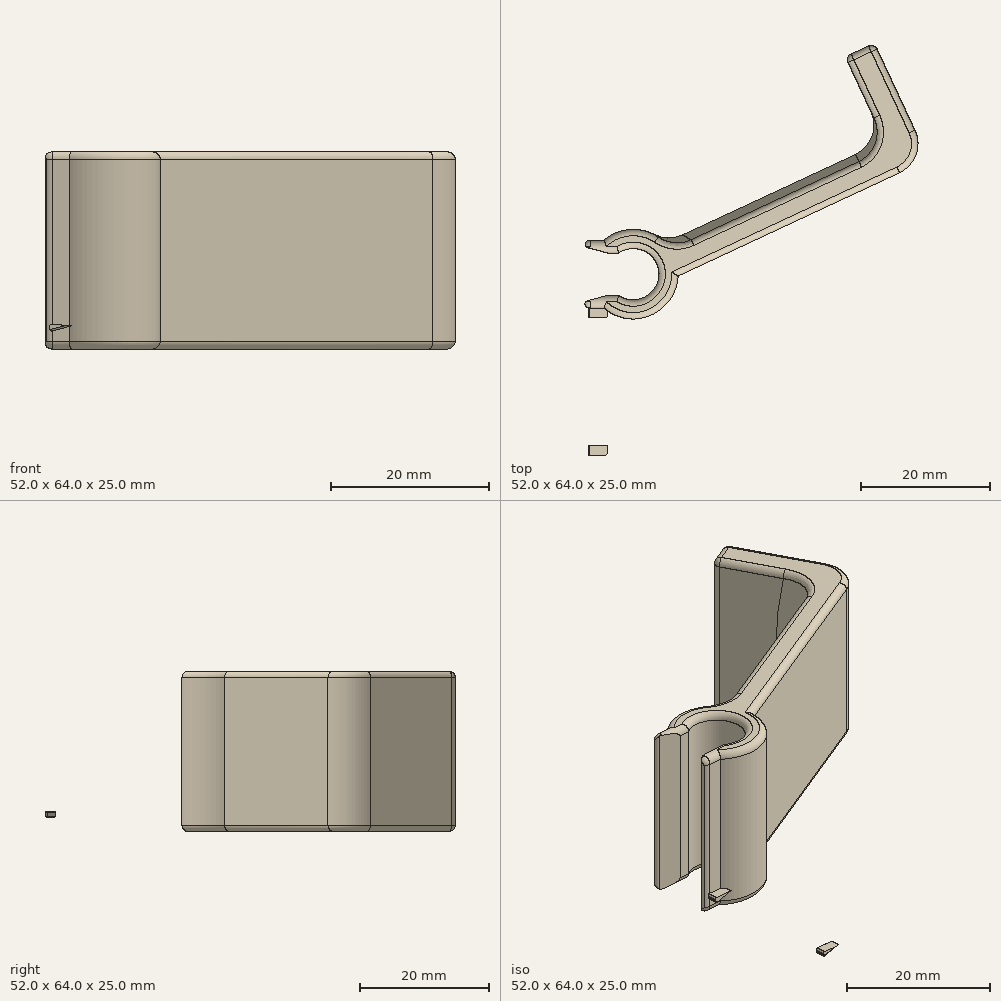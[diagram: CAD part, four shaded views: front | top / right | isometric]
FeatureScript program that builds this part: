
annotation { "Feature Type Name" : "Feature", "Feature Type Description" : "" }
export const myFeature = defineFeature(function(context is Context, id is Id, definition is map)
    precondition{}
    {
        {
            var Q0;
            Q0=qCreatedBy(makeId("Front.planeOp"),FACE);
            var sketch = newSketch(context, id + "F0", { "sketchPlane" : qUnion([Q0])});
            skCircle(sketch, "E0", {"center": v(0, 0) * mm, "radius": 7 * mm});
            skSolve(sketch);
        }
        {
            var Q0;
            Q0=makeQuery(id+"F0.imprint","IMPRINT",FACE,{"disambiguationData":[TD([[makeQuery(id+"F0.imprint","IMPRINT",EDGE,{"derivedFrom":sQuery(id+"F0.wireOp",EDGE,"E0")}),1.0]])]});
            extrude(context, id + "F1", {"entities" : qUnion([Q0]), "endBound" : BoundingType.SYMMETRIC, "depth" : 25 * mm, "offsetDistance" : 25 * mm});
        }
        {
            var Q0;
            Q0=makeQuery(id+"F1.opExtrude","CAP_FACE",FACE,{"disambiguationData":[OSD([sQuery(id+"F0.wireOp",EDGE,"E0")])],"isStart":false});
            var sketch = newSketch(context, id + "F2", { "sketchPlane" : qUnion([Q0])});
            skPoint(sketch, "E1", {"position": v(0, 0) * mm});
            skSolve(sketch);
        }
        {
            var Q0;
            Q0=sQuery(id+"F2.wireOp",VERTEX,"E1");
            var Q1;
            Q1=makeQuery(id+"F1.opExtrude","SWEPT_BODY",BODY,{"disambiguationData":[OSD([sQuery(id+"F0.wireOp",EDGE,"E0")])]});
            hole(context, id + "F3", {"style" : HoleStyle.SIMPLE, "endStyle" : HoleEndStyle.THROUGH, "holeDiameter" : 8 * mm, "isTappedThrough" : true, "tappedDepth" : 12 * mm, "tapClearance" : 3, "locations" : qUnion([Q0]), "scope" : qUnion([Q1]), "majorDiameter" : 5 * mm});
        }
        {
            var Q0;
            Q0=qCreatedBy(makeId("Right.planeOp"),FACE);
            var sketch = newSketch(context, id + "F4", { "sketchPlane" : qUnion([Q0])});
            skLineSegment(sketch, "E2.bottom", {"start": v(-25, 3.3) * mm, "end": v(25, 3.3) * mm});
            skLineSegment(sketch, "E2.top", {"start": v(-25, -3.3) * mm, "end": v(25, -3.3) * mm});
            skLineSegment(sketch, "E2.left", {"start": v(-25, 3.3) * mm, "end": v(-25, -3.3) * mm});
            skLineSegment(sketch, "E2.right", {"start": v(25, 3.3) * mm, "end": v(25, -3.3) * mm});
            skSolve(sketch);
        }
        {
            var Q0;
            Q0=makeQuery(id+"F4.imprint","IMPRINT",FACE,{"disambiguationData":[TD([[makeQuery(id+"F4.imprint","IMPRINT",EDGE,{"derivedFrom":sQuery(id+"F4.wireOp",EDGE,"E2.bottom")}),-1.0]])]});
            extrude(context, id + "F5", {"entities" : qUnion([Q0]), "operationType" : NewBodyOperationType.REMOVE, "oppositeDirection" : true, "depth" : 25 * mm, "offsetDistance" : 25 * mm});
        }
        {
            var Q0;
            Q0=makeQuery(id+"F1.opExtrude","SWEPT_BODY",BODY,{"disambiguationData":[OSD([sQuery(id+"F0.wireOp",EDGE,"E0")])]});
            var Q1;
            Q1=qCreatedBy(makeId("Right.planeOp"),FACE);
            transform(context, id + "F6", {"entities" : qUnion([Q0]), "transformType" : TransformType.TRANSLATION_DISTANCE, "transformDirection" : qUnion([Q1]), "distance" : 2.7 * mm, "makeCopy" : false});
        }
        {
            var Q0;
            Q0=qCreatedBy(makeId("Right.planeOp"),FACE);
            var sketch = newSketch(context, id + "F7", { "sketchPlane" : qUnion([Q0])});
            skLineSegment(sketch, "E3.bottom", {"start": v(12.5, 3.3) * mm, "end": v(-12.5, 3.3) * mm});
            skLineSegment(sketch, "E3.top", {"start": v(12.5, 5.3) * mm, "end": v(-12.5, 5.3) * mm});
            skLineSegment(sketch, "E3.left", {"start": v(12.5, 3.3) * mm, "end": v(12.5, 5.3) * mm});
            skLineSegment(sketch, "E3.right", {"start": v(-12.5, 3.3) * mm, "end": v(-12.5, 5.3) * mm});
            skLineSegment(sketch, "E4.bottom", {"start": v(-12.5, -3.3) * mm, "end": v(12.5, -3.3) * mm});
            skLineSegment(sketch, "E4.top", {"start": v(-12.5, -5.3) * mm, "end": v(12.5, -5.3) * mm});
            skLineSegment(sketch, "E4.left", {"start": v(-12.5, -3.3) * mm, "end": v(-12.5, -5.3) * mm});
            skLineSegment(sketch, "E4.right", {"start": v(12.5, -3.3) * mm, "end": v(12.5, -5.3) * mm});
            skSolve(sketch);
        }
        {
            var Q0;
            Q0=makeQuery(id+"F7.imprint","IMPRINT",FACE,{"disambiguationData":[TD([[makeQuery(id+"F7.imprint","IMPRINT",EDGE,{"derivedFrom":sQuery(id+"F7.wireOp",EDGE,"E3.bottom")}),-1.0]])]});
            var Q1;
            Q1=makeQuery(id+"F7.imprint","IMPRINT",FACE,{"disambiguationData":[TD([[makeQuery(id+"F7.imprint","IMPRINT",EDGE,{"derivedFrom":sQuery(id+"F7.wireOp",EDGE,"E4.bottom")}),-1.0]])]});
            extrude(context, id + "F8", {"entities" : qUnion([Q0, Q1]), "operationType" : NewBodyOperationType.ADD, "oppositeDirection" : true, "depth" : 5 * mm, "offsetDistance" : 25 * mm});
        }
        {
            var Q0;
            Q0=makeQuery(id+"F1.opExtrude","SWEPT_BODY",BODY,{"disambiguationData":[OSD([sQuery(id+"F0.wireOp",EDGE,"E0")])]});
            var Q1;
            Q1=qCreatedBy(makeId("Right.planeOp"),FACE);
            transform(context, id + "F9", {"entities" : qUnion([Q0]), "transformType" : TransformType.TRANSLATION_DISTANCE, "transformDirection" : qUnion([Q1]), "distance" : 8 * mm, "oppositeDirection" : true, "makeCopy" : false});
        }
        {
            var Q0;
            Q0=qCreatedBy(makeId("Right.planeOp"),FACE);
            var sketch = newSketch(context, id + "F10", { "sketchPlane" : qUnion([Q0])});
            skArc(sketch, "E5", {"start": v(12.5, 0) * mm, "mid": v(0, 1.45) * mm, "end": v(-12.5, 0) * mm});
            skLineSegment(sketch, "E6", {"start": v(-12.5, 0) * mm, "end": v(-12.5, -4.1) * mm});
            skLineSegment(sketch, "E7", {"start": v(-12.5, -4.1) * mm, "end": v(12.5, -4.1) * mm});
            skLineSegment(sketch, "E8", {"start": v(12.5, -4.1) * mm, "end": v(12.5, 0) * mm});
            skSolve(sketch);
        }
        {
            var Q0;
            Q0=makeQuery(id+"F10.imprint","IMPRINT",FACE,{"disambiguationData":[TD([[makeQuery(id+"F10.imprint","IMPRINT",EDGE,{"derivedFrom":sQuery(id+"F10.wireOp",EDGE,"E5")}),1.0]])]});
            extrude(context, id + "F11", {"entities" : qUnion([Q0]), "depth" : 45 * mm, "offsetDistance" : 25 * mm});
        }
        {
            var Q0;
            Q0=makeQuery(id+"F11.opExtrude","SWEPT_FACE",FACE,{"disambiguationData":[OSD([sQuery(id+"F10.wireOp",EDGE,"E7")])]});
            var sketch = newSketch(context, id + "F12", { "sketchPlane" : qUnion([Q0])});
            skLineSegment(sketch, "E9.bottom", {"start": v(45, 12.5) * mm, "end": v(40, 12.5) * mm});
            skLineSegment(sketch, "E9.top", {"start": v(45, -12.5) * mm, "end": v(40, -12.5) * mm});
            skLineSegment(sketch, "E9.left", {"start": v(45, 12.5) * mm, "end": v(45, -12.5) * mm});
            skLineSegment(sketch, "E9.right", {"start": v(40, 12.5) * mm, "end": v(40, -12.5) * mm});
            skSolve(sketch);
        }
        {
            var Q0;
            Q0=makeQuery(id+"F12.imprint","IMPRINT",FACE,{"disambiguationData":[TD([[makeQuery(id+"F12.imprint","IMPRINT",EDGE,{"derivedFrom":sQuery(id+"F12.wireOp",EDGE,"E9.bottom")}),1.0]])]});
            extrude(context, id + "F13", {"entities" : qUnion([Q0]), "operationType" : NewBodyOperationType.ADD, "oppositeDirection" : true, "depth" : 20 * mm, "offsetDistance" : 25 * mm});
        }
        {
            var Q0;
            Q0=makeQuery(id+"F11.opExtrude","SWEPT_BODY",BODY,{"disambiguationData":[OSD([sQuery(id+"F10.wireOp",EDGE,"E5"),sQuery(id+"F10.wireOp",EDGE,"E6"),sQuery(id+"F10.wireOp",EDGE,"E7"),sQuery(id+"F10.wireOp",EDGE,"E8")])]});
            var Q1;
            Q1=sQuery(id+"F10.wireOp",EDGE,"E7");
            transform(context, id + "F14", {"entities" : qUnion([Q0]), "transformType" : TransformType.ROTATION, "transformAxis" : qUnion([Q1]), "angle" : 25 * degree, "oppositeDirection" : true, "makeCopy" : false});
        }
        {
            var Q0;
            Q0=makeQuery(id+"F11.opExtrude","SWEPT_BODY",BODY,{"disambiguationData":[OSD([sQuery(id+"F10.wireOp",EDGE,"E5"),sQuery(id+"F10.wireOp",EDGE,"E6"),sQuery(id+"F10.wireOp",EDGE,"E7"),sQuery(id+"F10.wireOp",EDGE,"E8")])]});
            var Q1;
            Q1=qCreatedBy(makeId("Top.planeOp"),FACE);
            transform(context, id + "F15", {"entities" : qUnion([Q0]), "transformType" : TransformType.TRANSLATION_DISTANCE, "transformDirection" : qUnion([Q1]), "distance" : 3 * mm, "makeCopy" : false});
        }
        {
            var Q0;
            Q0=makeQuery(id+"F1.opExtrude","SWEPT_BODY",BODY,{"disambiguationData":[OSD([sQuery(id+"F0.wireOp",EDGE,"E0")])]});
            var Q1;
            Q1=makeQuery(id+"F11.opExtrude","SWEPT_BODY",BODY,{"disambiguationData":[OSD([sQuery(id+"F10.wireOp",EDGE,"E5"),sQuery(id+"F10.wireOp",EDGE,"E6"),sQuery(id+"F10.wireOp",EDGE,"E7"),sQuery(id+"F10.wireOp",EDGE,"E8")])]});
            booleanBodies(context, id + "F16", {"operationType" : BooleanOperationType.UNION, "tools" : qUnion([Q0, Q1])});
        }
        {
            var Q0;
            Q0=makeQuery(id+"F16.opBoolean","INTERSECT",EDGE,{"derivedFrom":[makeQuery(id+"F1.opExtrude","SWEPT_FACE",FACE,{"disambiguationData":[OSD([sQuery(id+"F0.wireOp",EDGE,"E0")])]}),makeQuery(id+"F11.opExtrude","SWEPT_FACE",FACE,{"disambiguationData":[OSD([sQuery(id+"F10.wireOp",EDGE,"E5")])]})]});
            var Q1;
            Q1=makeQuery(id+"F13.boolean.opBoolean","INTERSECT",EDGE,{"derivedFrom":[makeQuery(id+"F11.opExtrude","SWEPT_FACE",FACE,{"disambiguationData":[OSD([sQuery(id+"F10.wireOp",EDGE,"E5")])]}),makeQuery(id+"F13.opExtrude","SWEPT_FACE",FACE,{"disambiguationData":[OSD([sQuery(id+"F12.wireOp",EDGE,"E9.right")])]})]});
            var Q2;
            Q2=makeQuery(id+"F11.opExtrude","CAP_EDGE",EDGE,{"disambiguationData":[OSD([sQuery(id+"F10.wireOp",EDGE,"E7")])],"isStart":false});
            fillet(context, id + "F17", {"entities" : qUnion([Q0, Q1, Q2]), "radius" : 5 * mm, "tangentPropagation" : true, "allowEdgeOverflow" : false});
        }
        {
            var Q0;
            Q0=makeQuery(id+"F8.opExtrude","CAP_EDGE",EDGE,{"disambiguationData":[OSD([sQuery(id+"F7.wireOp",EDGE,"E3.top")])],"isStart":false});
            var Q1;
            Q1=makeQuery(id+"F8.opExtrude","CAP_EDGE",EDGE,{"disambiguationData":[OSD([sQuery(id+"F7.wireOp",EDGE,"E4.top")])],"isStart":false});
            var Q2;
            Q2=makeQuery(id+"F13.opExtrude","CAP_EDGE",EDGE,{"disambiguationData":[OSD([sQuery(id+"F12.wireOp",EDGE,"E9.right")])],"isStart":false});
            var Q3;
            Q3=makeQuery(id+"F13.opExtrude","CAP_EDGE",EDGE,{"disambiguationData":[OSD([sQuery(id+"F12.wireOp",EDGE,"E9.left")])],"isStart":false});
            var Q4;
            Q4=makeQuery(id+"F16.opBoolean","MERGE",FACE,{"derivedFrom":[makeQuery(id+"F8.boolean.opBoolean","MERGE",FACE,{"derivedFrom":[makeQuery(id+"F1.opExtrude","CAP_FACE",FACE,{"disambiguationData":[OSD([sQuery(id+"F0.wireOp",EDGE,"E0")])],"isStart":false}),makeQuery(id+"F8.opExtrude","SWEPT_FACE",FACE,{"disambiguationData":[OSD([sQuery(id+"F7.wireOp",EDGE,"E3.right")])]}),makeQuery(id+"F8.opExtrude","SWEPT_FACE",FACE,{"disambiguationData":[OSD([sQuery(id+"F7.wireOp",EDGE,"E4.left")])]})]}),makeQuery(id+"F13.boolean.opBoolean","MERGE",FACE,{"derivedFrom":[makeQuery(id+"F11.opExtrude","SWEPT_FACE",FACE,{"disambiguationData":[OSD([sQuery(id+"F10.wireOp",EDGE,"E6")])]}),makeQuery(id+"F13.opExtrude","SWEPT_FACE",FACE,{"disambiguationData":[OSD([sQuery(id+"F12.wireOp",EDGE,"E9.bottom")])]})]})]});
            var Q5;
            Q5=makeQuery(id+"F16.opBoolean","MERGE",FACE,{"derivedFrom":[makeQuery(id+"F8.boolean.opBoolean","MERGE",FACE,{"derivedFrom":[makeQuery(id+"F1.opExtrude","CAP_FACE",FACE,{"disambiguationData":[OSD([sQuery(id+"F0.wireOp",EDGE,"E0")])],"isStart":true}),makeQuery(id+"F8.opExtrude","SWEPT_FACE",FACE,{"disambiguationData":[OSD([sQuery(id+"F7.wireOp",EDGE,"E3.left")])]}),makeQuery(id+"F8.opExtrude","SWEPT_FACE",FACE,{"disambiguationData":[OSD([sQuery(id+"F7.wireOp",EDGE,"E4.right")])]})]}),makeQuery(id+"F13.boolean.opBoolean","MERGE",FACE,{"derivedFrom":[makeQuery(id+"F11.opExtrude","SWEPT_FACE",FACE,{"disambiguationData":[OSD([sQuery(id+"F10.wireOp",EDGE,"E8")])]}),makeQuery(id+"F13.opExtrude","SWEPT_FACE",FACE,{"disambiguationData":[OSD([sQuery(id+"F12.wireOp",EDGE,"E9.top")])]})]})]});
            fillet(context, id + "F18", {"entities" : qUnion([Q0, Q1, Q2, Q3, Q4, Q5]), "radius" : 1 * mm, "tangentPropagation" : true, "allowEdgeOverflow" : false});
        }
        {
            var Q0;
            Q0=makeQuery(id+"F8.opExtrude","CAP_EDGE",EDGE,{"disambiguationData":[OSD([sQuery(id+"F7.wireOp",EDGE,"E4.bottom")])],"isStart":false});
            var Q1;
            Q1=makeQuery(id+"F8.opExtrude","CAP_EDGE",EDGE,{"disambiguationData":[OSD([sQuery(id+"F7.wireOp",EDGE,"E3.bottom")])],"isStart":false});
            chamfer(context, id + "F19", {"entities" : qUnion([Q0, Q1]), "chamferType" : ChamferType.OFFSET_ANGLE, "width" : 1 * mm, "oppositeDirection" : false, "angle" : 75 * degree});
        }
        {
            var Q0;
            Q0=makeQuery(id+"F19.opChamfer","BLEND_EDGE",EDGE,{"blendedFrom":[makeQuery(id+"F8.opExtrude","CAP_EDGE",EDGE,{"disambiguationData":[OSD([sQuery(id+"F7.wireOp",EDGE,"E4.bottom")])],"isStart":false}),makeQuery(id+"F18.opFillet","BLEND_FACE",FACE,{"disambiguationData":[OSD([sQuery(id+"F7.wireOp",EDGE,"E4.top")])]})],"blendedInto":[makeQuery(id+"F18.opFillet","BLEND_FACE",FACE,{"disambiguationData":[OSD([sQuery(id+"F7.wireOp",EDGE,"E4.top")])]})]});
            var Q1;
            Q1=makeQuery(id+"F19.opChamfer","BLEND_EDGE",EDGE,{"blendedFrom":[makeQuery(id+"F8.opExtrude","CAP_EDGE",EDGE,{"disambiguationData":[OSD([sQuery(id+"F7.wireOp",EDGE,"E3.bottom")])],"isStart":false}),makeQuery(id+"F18.opFillet","BLEND_FACE",FACE,{"disambiguationData":[OSD([sQuery(id+"F7.wireOp",EDGE,"E3.top")])]})],"blendedInto":[makeQuery(id+"F18.opFillet","BLEND_FACE",FACE,{"disambiguationData":[OSD([sQuery(id+"F7.wireOp",EDGE,"E3.top")])]})]});
            fillet(context, id + "F20", {"entities" : qUnion([Q0, Q1]), "radius" : 0.5 * mm, "allowEdgeOverflow" : false});
        }
        {
            var Q0;
            Q0=qCreatedBy(makeId("Front.planeOp"),FACE);
            var sketch = newSketch(context, id + "F21", { "sketchPlane" : qUnion([Q0])});
            skLineSegment(sketch, "E10", {"start": v(-12.21, -4.09) * mm, "end": v(-9.27, -3.3) * mm});
            skLineSegment(sketch, "E11", {"start": v(-9.27, -3.3) * mm, "end": v(-12.42, -3.19) * mm});
            skLineSegment(sketch, "E12", {"start": v(-12.42, -3.19) * mm, "end": v(-12.21, -4.09) * mm});
            skSolve(sketch);
        }
        {
            var Q0;
            Q0=makeQuery(id+"F21.imprint","IMPRINT",FACE,{"disambiguationData":[TD([[makeQuery(id+"F21.imprint","IMPRINT",EDGE,{"derivedFrom":sQuery(id+"F21.wireOp",EDGE,"E10")}),1.0]])]});
            extrude(context, id + "F22", {"entities" : qUnion([Q0]), "depth" : 1.5 * mm, "offsetDistance" : 25 * mm});
        }
        {
            var Q0;
            Q0=makeQuery(id+"F22.opExtrude","SWEPT_BODY",BODY,{"disambiguationData":[OSD([sQuery(id+"F21.wireOp",EDGE,"E10"),sQuery(id+"F21.wireOp",EDGE,"E11"),sQuery(id+"F21.wireOp",EDGE,"E12")])]});
            var Q1;
            Q1=qCreatedBy(makeId("Front.planeOp"),FACE);
            transform(context, id + "F23", {"entities" : qUnion([Q0]), "transformType" : TransformType.TRANSLATION_DISTANCE, "transformDirection" : qUnion([Q1]), "distance" : 10 * mm, "makeCopy" : false});
        }
        {
            var Q0;
            Q0=makeQuery(id+"F22.opExtrude","SWEPT_BODY",BODY,{"disambiguationData":[OSD([sQuery(id+"F21.wireOp",EDGE,"E10"),sQuery(id+"F21.wireOp",EDGE,"E11"),sQuery(id+"F21.wireOp",EDGE,"E12")])]});
            var Q1;
            Q1=qCreatedBy(makeId("Front.planeOp"),FACE);
            mirror(context, id + "F24", {"entities" : qUnion([Q0]), "mirrorPlane" : qUnion([Q1])});
        }
        {
            var Q0;
            Q0=makeQuery(id+"F22.opExtrude","CAP_EDGE",EDGE,{"disambiguationData":[OSD([sQuery(id+"F21.wireOp",EDGE,"E10")])],"isStart":false});
            var Q1;
            Q1=makeQuery(id+"F22.opExtrude","SWEPT_EDGE",EDGE,{"disambiguationData":[OSD([sQuery(id+"F21.wireOp",EDGE,"E10"),sQuery(id+"F21.wireOp",EDGE,"E12")])]});
            var Q2;
            Q2=makeQuery(id+"F22.opExtrude","SWEPT_EDGE",EDGE,{"disambiguationData":[OSD([sQuery(id+"F21.wireOp",EDGE,"E11"),sQuery(id+"F21.wireOp",EDGE,"E12")])]});
            var Q3;
            Q3=makeQuery(id+"F24.opPattern","COPY",EDGE,{"derivedFrom":makeQuery(id+"F22.opExtrude","SWEPT_EDGE",EDGE,{"disambiguationData":[OSD([sQuery(id+"F21.wireOp",EDGE,"E11"),sQuery(id+"F21.wireOp",EDGE,"E12")])]}),"instanceName":"1"});
            var Q4;
            Q4=makeQuery(id+"F24.opPattern","COPY",EDGE,{"derivedFrom":makeQuery(id+"F22.opExtrude","SWEPT_EDGE",EDGE,{"disambiguationData":[OSD([sQuery(id+"F21.wireOp",EDGE,"E10"),sQuery(id+"F21.wireOp",EDGE,"E12")])]}),"instanceName":"1"});
            var Q5;
            Q5=makeQuery(id+"F24.opPattern","COPY",EDGE,{"derivedFrom":makeQuery(id+"F22.opExtrude","CAP_EDGE",EDGE,{"disambiguationData":[OSD([sQuery(id+"F21.wireOp",EDGE,"E10")])],"isStart":false}),"instanceName":"1"});
            fillet(context, id + "F25", {"entities" : qUnion([Q0, Q1, Q2, Q3, Q4, Q5]), "radius" : 0.25 * mm, "tangentPropagation" : true, "allowEdgeOverflow" : false});
        }
        {
            var Q0;
            Q0=makeQuery(id+"F1.opExtrude","SWEPT_BODY",BODY,{"disambiguationData":[OSD([sQuery(id+"F0.wireOp",EDGE,"E0")])]});
            var Q1;
            {var subQ0=sQuery(id+"F7.wireOp",EDGE,"E4.top");Q1=makeQuery(id+"F18.opFillet","BLEND_EDGE",EDGE,{"blendedFrom":[makeQuery(id+"F8.opExtrude","SWEPT_EDGE",EDGE,{"disambiguationData":[OSD([subQ0,sQuery(id+"F7.wireOp",EDGE,"E4.right")])]}),makeQuery(id+"F8.opExtrude","SWEPT_FACE",FACE,{"disambiguationData":[OSD([subQ0])]})],"blendedInto":[makeQuery(id+"F8.opExtrude","SWEPT_FACE",FACE,{"disambiguationData":[OSD([subQ0])]})]});}
            transform(context, id + "F26", {"entities" : qUnion([Q0]), "transformType" : TransformType.ROTATION, "transformAxis" : qUnion([Q1]), "angle" : 90 * degree, "oppositeDirection" : true, "makeCopy" : false});
        }
    });
